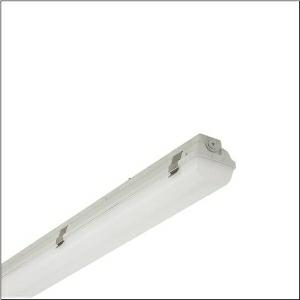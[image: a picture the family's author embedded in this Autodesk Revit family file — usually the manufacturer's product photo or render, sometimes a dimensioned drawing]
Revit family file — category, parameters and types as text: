
# Revit family: monsun_r__21_eco_51fj20mp47a_a802
name_source: partatom
category: Lighting Fixtures
units: mm (PartAtom-declared; Revit-internal decimal feet)

## family parameters
Cut with Voids When Loaded = No
Host = Face
Light Source = No
Part Type = Normal
Room Calculation Point = No
Round Connector Dimension = Use Diameter
Shared = No

## types (1)
- --- (1 x LED, 6600 lm, 50 W, 4000K)
    Apparent Load = 50 VA
    CIE Flux Codes = 40 69 88 88 100
    Color Rendering = 80
    Color Temperature = 4000K
    Default Elevation = 1800 mm
    Description = Monsun® 21 Eco, damp-proof luminaire, primary optical cover: diffuser, of PC, UV-stabilised, frosted, light emission: direct distribution, primary light characteristic: symmetric, installation type: suspended mounting, surface-mounted, LED, rated luminous flux: 6.600lm, luminous efficacy: 132lm/W, light colour: 840, colour temperature: 4000K, control gear: ECG Multilumen, with terminal, 3-pole, max. 2.5mm², mains connection: 220..240V, AC, 50/60Hz, rated input power: 50W, housing, of glass-fibre reinforced polyester, light grey (RAL 7035), length: 1.577mm, width: 90mm, height: 95mm, clip for enclosure, of spring steel V2A, protection rating (complete): IP66, insulation class (complete): insulation class I (protective earthing), certification: CE, UKCA, protection symbol: D, impact resistance: IK08, permissible operating ambient temperature: -20..+35°C, corresponds to IFS (International Featured Standards) requirements for safety and quality in the food industry, packaging unit: 1 piece
    Height = 103 mm
    Lamp = 1 x LED
    Lamp Light Flux = 6600 lm
    Lamp Power = 50 W
    Lamp count = 1
    Length = 1577 mm
    Luminous efficacy = 132 lm/W
    Manufacturer = Siteco
    ModVariant = No
    Model = 51FJ20MP47A
    Mounting Place = Ceiling
    Mounting Type = Surface mounted
    Number of Poles = 1
    OnlyDefault = Yes
    Power Factor = 1
    Product Name = Monsun® 21 Eco
    Product group = damp-proof luminaire | ceiling mounted
    ProductGroupID = 300
    Protection Class = Protection class I
    Protection Degree = IP 66
    RLX_Detail_Level = 1
    RlxData = <blob elided: 33881 chars, md5=ad7e09b0>
    Socket = socket
    Standby Power = 0 W
    System Light Flux = 6600 lm
    System Power = 50 W
    Type Comments = factory setting: luminous flux: 100 % | (ON | ON) | 350 mA
    Type Image = l_1007218.jpg
    URL = http://relux.com
    VarID = @adj_055445
    Voltage = 0 V
    Weight = 0.00 kg
    Width = 90 mm

## geometry (parser evidence)
native form markers: Blend x4, Sweep x13
no freeform markers — native parametric forms only
